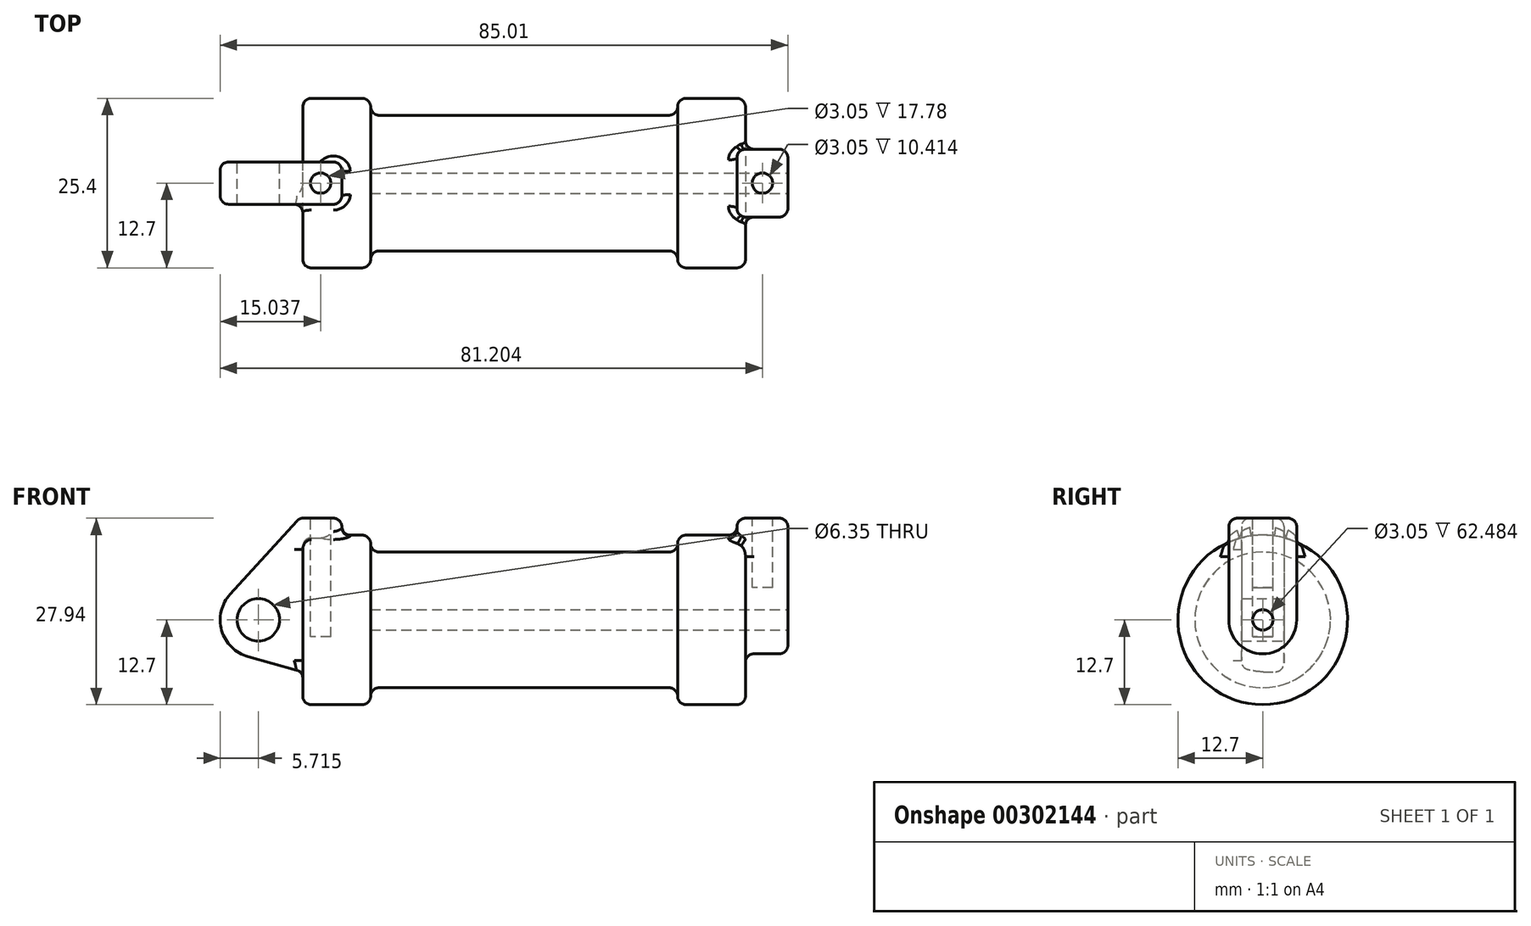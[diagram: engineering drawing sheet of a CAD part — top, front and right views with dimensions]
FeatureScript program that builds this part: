
annotation { "Feature Type Name" : "Feature", "Feature Type Description" : "" }
export const myFeature = defineFeature(function(context is Context, id is Id, definition is map)
    precondition{}
    {
        {
            var Q0;
            Q0=qCreatedBy(makeId("Front.planeOp"),FACE);
            var sketch = newSketch(context, id + "F0", { "sketchPlane" : qUnion([Q0])});
            skLineSegment(sketch, "E0", {"start": v(0, 0) * mm, "end": v(0, 12.7) * mm});
            skLineSegment(sketch, "E1", {"start": v(0, 12.7) * mm, "end": v(10.16, 12.7) * mm});
            skLineSegment(sketch, "E2", {"start": v(10.16, 12.7) * mm, "end": v(10.16, 10.16) * mm});
            skLineSegment(sketch, "E3", {"start": v(10.16, 10.16) * mm, "end": v(56.13, 10.16) * mm});
            skLineSegment(sketch, "E4", {"start": v(56.13, 10.16) * mm, "end": v(56.13, 12.7) * mm});
            skLineSegment(sketch, "E5", {"start": v(56.13, 12.7) * mm, "end": v(66.3, 12.7) * mm});
            skLineSegment(sketch, "E6", {"start": v(66.3, 12.7) * mm, "end": v(66.3, 0) * mm});
            skLineSegment(sketch, "E7", {"start": v(66.3, 0) * mm, "end": v(0, 0) * mm});
            skLineSegment(sketch, "E8", {"start": v(5.84, 15.24) * mm, "end": v(-0.5, 15.24) * mm});
            skLineSegment(sketch, "E9", {"start": v(-0.5, 15.24) * mm, "end": v(-10.88, 3.85) * mm});
            skLineSegment(sketch, "E10", {"start": v(0, 0) * mm, "end": v(-6.65, 0) * mm});
            skCircle(sketch, "E11", {"center": v(-6.65, 0) * mm, "radius": 5.72 * mm});
            skCircle(sketch, "E12", {"center": v(-6.65, 0) * mm, "radius": 3.18 * mm});
            skLineSegment(sketch, "E13", {"start": v(5.84, 15.24) * mm, "end": v(5.84, -9.4) * mm});
            skLineSegment(sketch, "E14", {"start": v(5.84, -9.4) * mm, "end": v(-8.18, -5.5) * mm});
            skSolve(sketch);
        }
        {
            var Q0;
            {var subQ0=sQuery(id+"F0.wireOp",EDGE,"E2");Q0=makeQuery(id+"F0.imprint","IMPRINT",FACE,{"disambiguationData":[TD([[makeQuery(id+"F0.imprint","IMPRINT",EDGE,{"derivedFrom":subQ0}),-1.0]])]});}
            var Q1;
            {var subQ0=sQuery(id+"F0.wireOp",EDGE,"E0");Q1=makeQuery(id+"F0.imprint","IMPRINT",FACE,{"disambiguationData":[TD([[makeQuery(id+"F0.imprint","IMPRINT",EDGE,{"derivedFrom":subQ0}),-1.0]])]});}
            var Q2;
            Q2=sQuery(id+"F0.wireOp",EDGE,"E7");
            revolve(context, id + "F1", {"entities" : qUnion([Q0, Q1]), "axis" : qUnion([Q2]), "revolveType" : RevolveType.FULL});
        }
        {
            var Q0;
            {var subQ1=sQuery(id+"F0.wireOp",EDGE,"E0");Q0=makeQuery(id+"F0.imprint","IMPRINT",FACE,{"disambiguationData":[TD([[makeQuery(id+"F0.imprint","IMPRINT",EDGE,{"derivedFrom":subQ1}),1.0]])]});}
            var Q1;
            Q1=makeQuery(id+"F0.imprint","IMPRINT",FACE,{"disambiguationData":[TD([[makeQuery(id+"F0.imprint","IMPRINT",EDGE,{"derivedFrom":sQuery(id+"F0.wireOp",EDGE,"E12")}),-1.0]])]});
            var Q2;
            {var subQ0=sQuery(id+"F0.wireOp",EDGE,"E14");Q2=makeQuery(id+"F0.imprint","IMPRINT",FACE,{"disambiguationData":[TD([[makeQuery(id+"F0.imprint","IMPRINT",EDGE,{"derivedFrom":subQ0}),-1.0]])]});}
            var Q3;
            {var subQ0=sQuery(id+"F0.wireOp",EDGE,"E0");Q3=makeQuery(id+"F0.imprint","IMPRINT",FACE,{"disambiguationData":[TD([[makeQuery(id+"F0.imprint","IMPRINT",EDGE,{"derivedFrom":subQ0}),-1.0]])]});}
            extrude(context, id + "F2", {"entities" : qUnion([Q0, Q1, Q2, Q3]), "operationType" : NewBodyOperationType.ADD, "endBound" : BoundingType.SYMMETRIC, "depth" : 6.35 * mm});
        }
        {
            var Q0;
            Q0=makeQuery(id+"F1.opRevolve","SWEPT_FACE",FACE,{"disambiguationData":[OSD([sQuery(id+"F0.wireOp",EDGE,"E6")])]});
            var sketch = newSketch(context, id + "F3", { "sketchPlane" : qUnion([Q0])});
            skCircle(sketch, "E15", {"center": v(0, 0) * mm, "radius": 1.52 * mm});
            skCircle(sketch, "E16", {"center": v(0, 0) * mm, "radius": 5.08 * mm});
            skLineSegment(sketch, "E17", {"start": v(5.08, 0) * mm, "end": v(5.08, 15.24) * mm});
            skLineSegment(sketch, "E18.MirrorCS", {"start": v(-5.08, 0) * mm, "end": v(-5.08, 15.24) * mm});
            skLineSegment(sketch, "E19", {"start": v(5.08, 15.24) * mm, "end": v(-5.08, 15.24) * mm});
            skSolve(sketch);
        }
        {
            var Q0;
            Q0=makeQuery(id+"F3.imprint","IMPRINT",FACE,{"disambiguationData":[TD([[makeQuery(id+"F3.imprint","IMPRINT",EDGE,{"derivedFrom":sQuery(id+"F3.wireOp",EDGE,"E15")}),-1.0]])]});
            var Q1;
            {var subQ0=sQuery(id+"F3.wireOp",EDGE,"E17");var subQ1=sQuery(id+"F3.wireOp",EDGE,"E16");var subQ2=makeQuery(id+"F3.imprint","INTERSECT",VERTEX,{"derivedFrom":[subQ1,subQ0]});Q1=makeQuery(id+"F3.imprint","IMPRINT",FACE,{"disambiguationData":[TD([[makeQuery(id+"F3.imprint","IMPRINT",EDGE,{"disambiguationData":[TD([[subQ2,-1.0]])],"derivedFrom":subQ1}),-1.0]])]});}
            var Q2;
            {var subQ0=sQuery(id+"F3.wireOp",EDGE,"E19");Q2=makeQuery(id+"F3.imprint","IMPRINT",FACE,{"disambiguationData":[TD([[makeQuery(id+"F3.imprint","IMPRINT",EDGE,{"derivedFrom":subQ0}),1.0]])]});}
            extrude(context, id + "F4", {"entities" : qUnion([Q0, Q1, Q2]), "operationType" : NewBodyOperationType.ADD, "oppositeDirection" : true, "depth" : 1.27 * mm, "hasSecondDirection" : true, "secondDirectionOppositeDirection" : false, "secondDirectionDepth" : 6.35 * mm});
        }
        {
            var Q0;
            Q0=makeQuery(id+"F3.imprint","IMPRINT",FACE,{"disambiguationData":[TD([[makeQuery(id+"F3.imprint","IMPRINT",EDGE,{"derivedFrom":sQuery(id+"F3.wireOp",EDGE,"E15")}),1.0]])]});
            var Q1;
            Q1=makeQuery(id+"F1.opRevolve","SWEPT_FACE",FACE,{"disambiguationData":[OSD([sQuery(id+"F0.wireOp",EDGE,"E2")])]});
            extrude(context, id + "F5", {"entities" : qUnion([Q0]), "operationType" : NewBodyOperationType.REMOVE, "endBound" : BoundingType.UP_TO_SURFACE, "oppositeDirection" : true, "endBoundEntityFace" : qUnion([Q1]), "depth" : 25.4 * mm});
        }
        {
            var Q0;
            Q0=makeQuery(id+"F2.opExtrude","SWEPT_FACE",FACE,{"disambiguationData":[OSD([sQuery(id+"F0.wireOp",EDGE,"E8")])]});
            var Q1;
            Q1=makeQuery(id+"F4.opExtrude","SWEPT_FACE",FACE,{"disambiguationData":[OSD([sQuery(id+"F3.wireOp",EDGE,"E19")])]});
            cPlane(context, id + "F6", {"entities" : qUnion([Q0, Q1]), "cplaneType" : CPlaneType.MID_PLANE, "offset" : 25.4 * mm, "width" : 152.4 * mm, "height" : 152.4 * mm});
        }
        {
            var Q0;
            Q0=qCreatedBy(id+"F6.planeOp",FACE);
            var sketch = newSketch(context, id + "F7", { "sketchPlane" : qUnion([Q0])});
            skCircle(sketch, "E20", {"center": v(2.67, 0) * mm, "radius": 1.52 * mm});
            skPoint(sketch, "E21", {"position": v(68.83, 0) * mm});
            skCircle(sketch, "E22", {"center": v(68.83, 0) * mm, "radius": 1.52 * mm});
            skSolve(sketch);
        }
        {
            var Q0;
            Q0=makeQuery(id+"F7.imprint","IMPRINT",FACE,{"disambiguationData":[TD([[makeQuery(id+"F7.imprint","IMPRINT",EDGE,{"derivedFrom":sQuery(id+"F7.wireOp",EDGE,"E20")}),1.0]])]});
            extrude(context, id + "F8", {"entities" : qUnion([Q0]), "operationType" : NewBodyOperationType.REMOVE, "oppositeDirection" : true, "depth" : 17.78 * mm});
        }
        {
            var Q0;
            Q0=makeQuery(id+"F7.imprint","IMPRINT",FACE,{"disambiguationData":[TD([[makeQuery(id+"F7.imprint","IMPRINT",EDGE,{"derivedFrom":sQuery(id+"F7.wireOp",EDGE,"E22")}),1.0]])]});
            extrude(context, id + "F9", {"entities" : qUnion([Q0]), "operationType" : NewBodyOperationType.REMOVE, "oppositeDirection" : true, "depth" : 10.4 * mm});
        }
        {
            var Q0;
            Q0=makeQuery(id+"F1.opRevolve","SWEPT_EDGE",EDGE,{"disambiguationData":[OSD([sQuery(id+"F0.wireOp",EDGE,"E5"),sQuery(id+"F0.wireOp",EDGE,"E6")])]});
            var Q1;
            Q1=makeQuery(id+"F1.opRevolve","SWEPT_EDGE",EDGE,{"disambiguationData":[OSD([sQuery(id+"F0.wireOp",EDGE,"E4"),sQuery(id+"F0.wireOp",EDGE,"E5")])]});
            var Q2;
            Q2=makeQuery(id+"F1.opRevolve","SWEPT_EDGE",EDGE,{"disambiguationData":[OSD([sQuery(id+"F0.wireOp",EDGE,"E3"),sQuery(id+"F0.wireOp",EDGE,"E4")])]});
            var Q3;
            Q3=makeQuery(id+"F1.opRevolve","SWEPT_EDGE",EDGE,{"disambiguationData":[OSD([sQuery(id+"F0.wireOp",EDGE,"E1"),sQuery(id+"F0.wireOp",EDGE,"E2")])]});
            var Q4;
            Q4=makeQuery(id+"F1.opRevolve","SWEPT_EDGE",EDGE,{"disambiguationData":[OSD([sQuery(id+"F0.wireOp",EDGE,"E0"),sQuery(id+"F0.wireOp",EDGE,"E1")])]});
            var Q5;
            Q5=makeQuery(id+"F1.opRevolve","SWEPT_EDGE",EDGE,{"disambiguationData":[OSD([sQuery(id+"F0.wireOp",EDGE,"E2"),sQuery(id+"F0.wireOp",EDGE,"E3")])]});
            fillet(context, id + "F10", {"entities" : qUnion([Q0, Q1, Q2, Q3, Q4, Q5]), "radius" : 1.27 * mm, "tangentPropagation" : true, "allowEdgeOverflow" : false});
        }
        {
            var Q0;
            Q0=makeQuery(id+"F4.opExtrude","SWEPT_EDGE",EDGE,{"disambiguationData":[OSD([sQuery(id+"F3.wireOp",EDGE,"E18.MirrorCS"),sQuery(id+"F3.wireOp",EDGE,"E19")])]});
            var Q1;
            Q1=makeQuery(id+"F4.opExtrude","CAP_EDGE",EDGE,{"disambiguationData":[OSD([sQuery(id+"F3.wireOp",EDGE,"E19")])],"isStart":true});
            var Q2;
            Q2=makeQuery(id+"F4.opExtrude","CAP_EDGE",EDGE,{"disambiguationData":[OSD([sQuery(id+"F3.wireOp",EDGE,"E18.MirrorCS")])],"isStart":true});
            var Q3;
            Q3=makeQuery(id+"F4.opExtrude","CAP_EDGE",EDGE,{"disambiguationData":[OSD([sQuery(id+"F3.wireOp",EDGE,"E19")])],"isStart":false});
            var Q4;
            Q4=makeQuery(id+"F4.opExtrude","SWEPT_EDGE",EDGE,{"disambiguationData":[OSD([sQuery(id+"F3.wireOp",EDGE,"E17"),sQuery(id+"F3.wireOp",EDGE,"E19")])]});
            var Q5;
            Q5=makeQuery(id+"F4.boolean.opBoolean","INTERSECT",EDGE,{"derivedFrom":[makeQuery(id+"F1.opRevolve","SWEPT_FACE",FACE,{"disambiguationData":[OSD([sQuery(id+"F0.wireOp",EDGE,"E5")])]}),makeQuery(id+"F4.opExtrude","CAP_FACE",FACE,{"disambiguationData":[OSD([sQuery(id+"F3.wireOp",EDGE,"E15"),sQuery(id+"F3.wireOp",EDGE,"E16"),sQuery(id+"F3.wireOp",EDGE,"E17"),sQuery(id+"F3.wireOp",EDGE,"E18.MirrorCS"),sQuery(id+"F3.wireOp",EDGE,"E19")])],"isStart":false})]});
            var Q6;
            Q6=makeQuery(id+"F10.opFillet","BLEND_EDGE",EDGE,{"blendedFrom":[makeQuery(id+"F1.opRevolve","SWEPT_EDGE",EDGE,{"disambiguationData":[OSD([sQuery(id+"F0.wireOp",EDGE,"E5"),sQuery(id+"F0.wireOp",EDGE,"E6")])]}),makeQuery(id+"F4.opExtrude","SWEPT_FACE",FACE,{"disambiguationData":[OSD([sQuery(id+"F3.wireOp",EDGE,"E17")])]})],"blendedInto":[makeQuery(id+"F4.opExtrude","SWEPT_FACE",FACE,{"disambiguationData":[OSD([sQuery(id+"F3.wireOp",EDGE,"E17")])]})]});
            var Q7;
            Q7=makeQuery(id+"F4.opExtrude","CAP_EDGE",EDGE,{"disambiguationData":[OSD([sQuery(id+"F3.wireOp",EDGE,"E18.MirrorCS")])],"isStart":false});
            var Q8;
            Q8=makeQuery(id+"F4.opExtrude","CAP_EDGE",EDGE,{"disambiguationData":[OSD([sQuery(id+"F3.wireOp",EDGE,"E17")])],"isStart":false});
            fillet(context, id + "F11", {"entities" : qUnion([Q0, Q1, Q2, Q3, Q4, Q5, Q6, Q7, Q8]), "radius" : 1.27 * mm, "tangentPropagation" : true, "allowEdgeOverflow" : false});
        }
        {
            var Q0;
            Q0=makeQuery(id+"F2.opExtrude","CAP_EDGE",EDGE,{"disambiguationData":[OSD([sQuery(id+"F0.wireOp",EDGE,"E9")])],"isStart":true});
            var Q1;
            Q1=makeQuery(id+"F2.opExtrude","CAP_EDGE",EDGE,{"disambiguationData":[OSD([sQuery(id+"F0.wireOp",EDGE,"E9")])],"isStart":false});
            var Q2;
            Q2=makeQuery(id+"F2.opExtrude","CAP_EDGE",EDGE,{"disambiguationData":[OSD([sQuery(id+"F0.wireOp",EDGE,"E8")])],"isStart":false});
            var Q3;
            Q3=makeQuery(id+"F2.opExtrude","CAP_EDGE",EDGE,{"disambiguationData":[OSD([sQuery(id+"F0.wireOp",EDGE,"E8")])],"isStart":true});
            var Q4;
            Q4=makeQuery(id+"F2.opExtrude","SWEPT_EDGE",EDGE,{"disambiguationData":[OSD([sQuery(id+"F0.wireOp",EDGE,"E8"),sQuery(id+"F0.wireOp",EDGE,"E13")])]});
            var Q5;
            Q5=makeQuery(id+"F2.boolean.opBoolean","INTERSECT",EDGE,{"derivedFrom":[makeQuery(id+"F1.opRevolve","SWEPT_FACE",FACE,{"disambiguationData":[OSD([sQuery(id+"F0.wireOp",EDGE,"E0")])]}),makeQuery(id+"F2.opExtrude","CAP_FACE",FACE,{"disambiguationData":[OSD([sQuery(id+"F0.wireOp",EDGE,"E8"),sQuery(id+"F0.wireOp",EDGE,"E9"),sQuery(id+"F0.wireOp",EDGE,"E11"),sQuery(id+"F0.wireOp",EDGE,"E12"),sQuery(id+"F0.wireOp",EDGE,"E13"),sQuery(id+"F0.wireOp",EDGE,"E14")])],"isStart":false})]});
            var Q6;
            Q6=makeQuery(id+"F2.boolean.opBoolean","INTERSECT",EDGE,{"derivedFrom":[makeQuery(id+"F1.opRevolve","SWEPT_FACE",FACE,{"disambiguationData":[OSD([sQuery(id+"F0.wireOp",EDGE,"E1")])]}),makeQuery(id+"F2.opExtrude","SWEPT_FACE",FACE,{"disambiguationData":[OSD([sQuery(id+"F0.wireOp",EDGE,"E13")])]})]});
            var Q7;
            Q7=makeQuery(id+"F2.opExtrude","CAP_EDGE",EDGE,{"disambiguationData":[OSD([sQuery(id+"F0.wireOp",EDGE,"E13")])],"isStart":false});
            var Q8;
            Q8=makeQuery(id+"F2.opExtrude","CAP_EDGE",EDGE,{"disambiguationData":[OSD([sQuery(id+"F0.wireOp",EDGE,"E13")])],"isStart":true});
            var Q9;
            Q9=makeQuery(id+"F2.opExtrude","SWEPT_EDGE",EDGE,{"disambiguationData":[OSD([sQuery(id+"F0.wireOp",EDGE,"E8"),sQuery(id+"F0.wireOp",EDGE,"E9")])]});
            fillet(context, id + "F12", {"entities" : qUnion([Q0, Q1, Q2, Q3, Q4, Q5, Q6, Q7, Q8, Q9]), "radius" : 1.27 * mm, "tangentPropagation" : true, "allowEdgeOverflow" : false});
        }
    });
